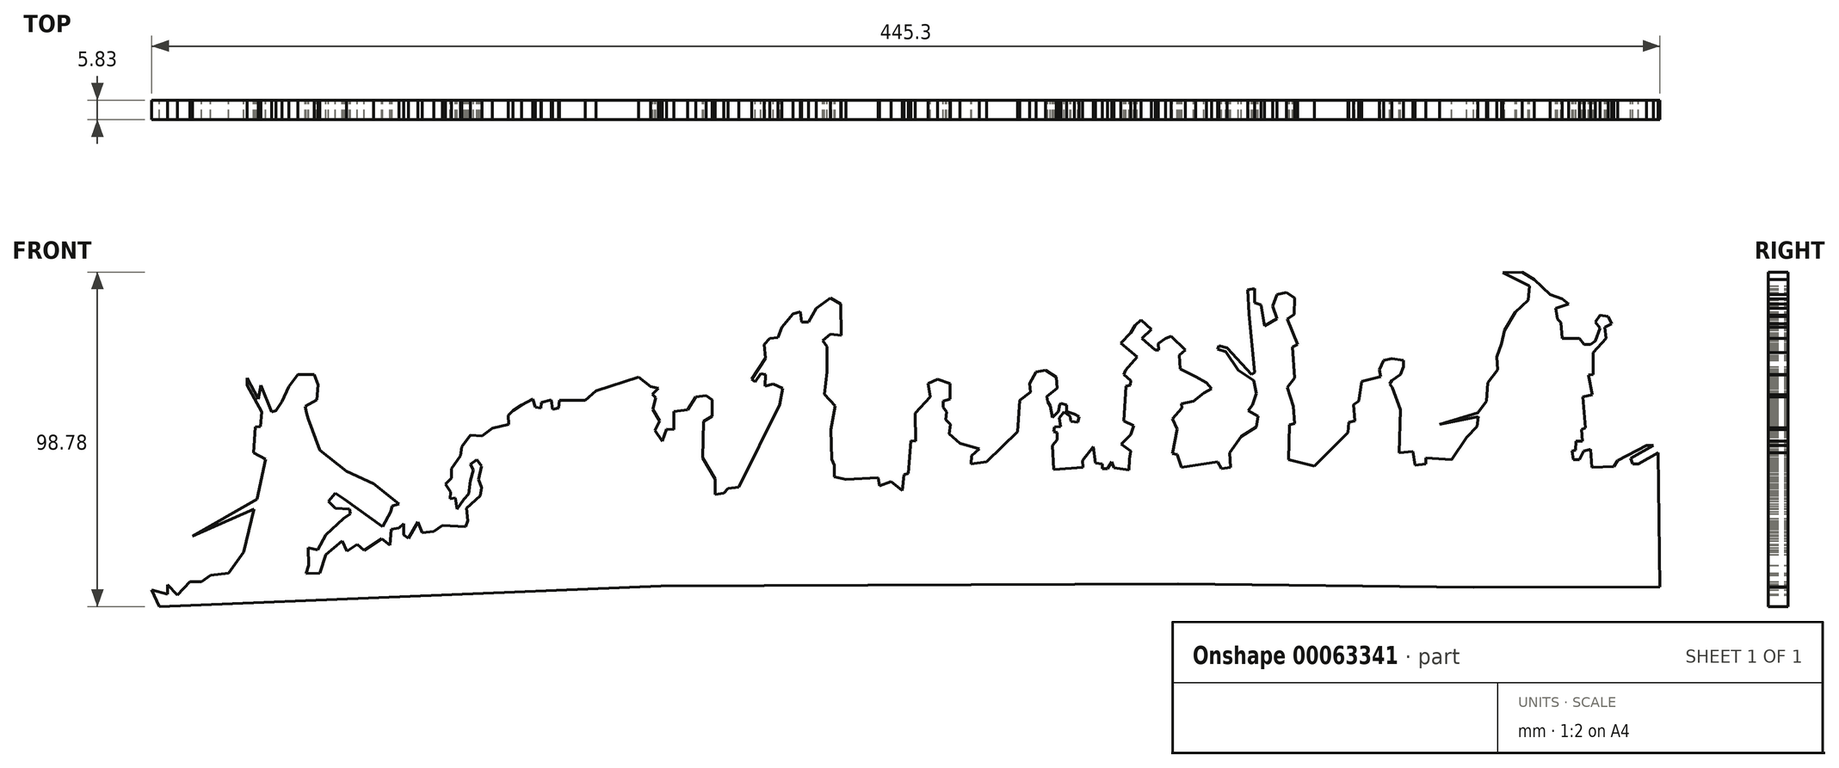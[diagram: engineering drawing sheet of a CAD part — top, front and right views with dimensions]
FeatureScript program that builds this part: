
annotation { "Feature Type Name" : "Feature", "Feature Type Description" : "" }
export const myFeature = defineFeature(function(context is Context, id is Id, definition is map)
    precondition{}
    {
        {
            var Q0;
            Q0=qCreatedBy(makeId("Front.planeOp"),FACE);
            var sketch = newSketch(context, id + "F0", { "sketchPlane" : qUnion([Q0])});
            skLineSegment(sketch, "E0", {"start": v(167.62, -43.74) * mm, "end": v(222.65, -43.54) * mm});
            skLineSegment(sketch, "E1", {"start": v(222.65, -43.54) * mm, "end": v(222.05, -4.03) * mm});
            skLineSegment(sketch, "E2", {"start": v(222.05, -4.03) * mm, "end": v(216.2, -7.26) * mm});
            skLineSegment(sketch, "E3", {"start": v(216.2, -7.26) * mm, "end": v(214.59, -7.26) * mm});
            skLineSegment(sketch, "E4", {"start": v(214.59, -7.26) * mm, "end": v(213.98, -5.64) * mm});
            skLineSegment(sketch, "E5", {"start": v(213.98, -5.64) * mm, "end": v(220.64, -1.81) * mm});
            skLineSegment(sketch, "E6", {"start": v(220.64, -1.81) * mm, "end": v(218.62, -1.81) * mm});
            skLineSegment(sketch, "E7", {"start": v(218.62, -1.81) * mm, "end": v(210.15, -6.25) * mm});
            skLineSegment(sketch, "E8", {"start": v(210.15, -6.25) * mm, "end": v(208.95, -8.06) * mm});
            skLineSegment(sketch, "E9", {"start": v(208.95, -8.06) * mm, "end": v(202.5, -8.27) * mm});
            skLineSegment(sketch, "E10", {"start": v(202.5, -8.27) * mm, "end": v(202.1, -3.02) * mm});
            skLineSegment(sketch, "E11", {"start": v(202.1, -3.02) * mm, "end": v(200.08, -3.43) * mm});
            skLineSegment(sketch, "E12", {"start": v(200.08, -3.43) * mm, "end": v(198.87, -6.05) * mm});
            skLineSegment(sketch, "E13", {"start": v(198.87, -6.05) * mm, "end": v(197.05, -6.05) * mm});
            skLineSegment(sketch, "E14", {"start": v(197.05, -6.05) * mm, "end": v(196.65, -3.43) * mm});
            skLineSegment(sketch, "E15", {"start": v(196.65, -3.43) * mm, "end": v(197.66, -3.23) * mm});
            skLineSegment(sketch, "E16", {"start": v(197.66, -3.23) * mm, "end": v(197.86, -0.6) * mm});
            skLineSegment(sketch, "E17", {"start": v(197.86, -0.6) * mm, "end": v(199.67, -0.6) * mm});
            skLineSegment(sketch, "E18", {"start": v(199.67, -0.6) * mm, "end": v(199.47, 2.82) * mm});
            skLineSegment(sketch, "E19", {"start": v(199.47, 2.82) * mm, "end": v(200.68, 3.43) * mm});
            skLineSegment(sketch, "E20", {"start": v(200.68, 3.43) * mm, "end": v(199.87, 12.5) * mm});
            skLineSegment(sketch, "E21", {"start": v(199.87, 12.5) * mm, "end": v(202.7, 13.1) * mm});
            skLineSegment(sketch, "E22", {"start": v(202.7, 13.1) * mm, "end": v(201.49, 18.95) * mm});
            skLineSegment(sketch, "E23", {"start": v(201.49, 18.95) * mm, "end": v(202.9, 19.15) * mm});
            skLineSegment(sketch, "E24", {"start": v(202.9, 19.15) * mm, "end": v(202.9, 25.6) * mm});
            skLineSegment(sketch, "E25", {"start": v(202.9, 25.6) * mm, "end": v(206.73, 29.83) * mm});
            skLineSegment(sketch, "E26", {"start": v(206.73, 29.83) * mm, "end": v(206.32, 33.06) * mm});
            skLineSegment(sketch, "E27", {"start": v(206.32, 33.06) * mm, "end": v(208.34, 34.07) * mm});
            skLineSegment(sketch, "E28", {"start": v(208.34, 34.07) * mm, "end": v(207.33, 36.29) * mm});
            skLineSegment(sketch, "E29", {"start": v(207.33, 36.29) * mm, "end": v(204.91, 36.69) * mm});
            skLineSegment(sketch, "E30", {"start": v(204.91, 36.69) * mm, "end": v(203.5, 34.67) * mm});
            skLineSegment(sketch, "E31", {"start": v(203.5, 34.67) * mm, "end": v(204.91, 32.86) * mm});
            skLineSegment(sketch, "E32", {"start": v(204.91, 32.86) * mm, "end": v(203.5, 29.03) * mm});
            skLineSegment(sketch, "E33", {"start": v(203.5, 29.03) * mm, "end": v(202.1, 28.02) * mm});
            skLineSegment(sketch, "E34", {"start": v(202.1, 28.02) * mm, "end": v(200.28, 28.02) * mm});
            skLineSegment(sketch, "E35", {"start": v(200.28, 28.02) * mm, "end": v(198.87, 29.83) * mm});
            skLineSegment(sketch, "E36", {"start": v(198.87, 29.83) * mm, "end": v(193.83, 29.83) * mm});
            skLineSegment(sketch, "E37", {"start": v(193.83, 29.83) * mm, "end": v(193.42, 34.47) * mm});
            skLineSegment(sketch, "E38", {"start": v(193.42, 34.47) * mm, "end": v(192.42, 35.48) * mm});
            skLineSegment(sketch, "E39", {"start": v(192.42, 35.48) * mm, "end": v(191.81, 38.7) * mm});
            skLineSegment(sketch, "E40", {"start": v(191.81, 38.7) * mm, "end": v(195.64, 39.91) * mm});
            skLineSegment(sketch, "E41", {"start": v(195.64, 39.91) * mm, "end": v(193.83, 41.53) * mm});
            skLineSegment(sketch, "E42", {"start": v(193.83, 41.53) * mm, "end": v(190.2, 42.74) * mm});
            skLineSegment(sketch, "E43", {"start": v(190.2, 42.74) * mm, "end": v(185.56, 47.17) * mm});
            skLineSegment(sketch, "E44", {"start": v(185.56, 47.17) * mm, "end": v(181.93, 49.39) * mm});
            skLineSegment(sketch, "E45", {"start": v(181.93, 49.39) * mm, "end": v(176.29, 49.19) * mm});
            skLineSegment(sketch, "E46", {"start": v(176.29, 49.19) * mm, "end": v(180.32, 47.17) * mm});
            skLineSegment(sketch, "E47", {"start": v(180.32, 47.17) * mm, "end": v(184.15, 45.36) * mm});
            skLineSegment(sketch, "E48", {"start": v(184.15, 45.36) * mm, "end": v(183.75, 41.12) * mm});
            skLineSegment(sketch, "E49", {"start": v(183.75, 41.12) * mm, "end": v(179.92, 37.5) * mm});
            skLineSegment(sketch, "E50", {"start": v(179.92, 37.5) * mm, "end": v(176.7, 32.25) * mm});
            skLineSegment(sketch, "E51", {"start": v(176.7, 32.25) * mm, "end": v(175.88, 28.22) * mm});
            skLineSegment(sketch, "E52", {"start": v(175.88, 28.22) * mm, "end": v(174.47, 24.4) * mm});
            skLineSegment(sketch, "E53", {"start": v(174.47, 24.4) * mm, "end": v(174.68, 20.56) * mm});
            skLineSegment(sketch, "E54", {"start": v(174.68, 20.56) * mm, "end": v(171.85, 16.73) * mm});
            skLineSegment(sketch, "E55", {"start": v(171.85, 16.73) * mm, "end": v(171.45, 11.29) * mm});
            skLineSegment(sketch, "E56", {"start": v(171.45, 11.29) * mm, "end": v(168.83, 7.86) * mm});
            skLineSegment(sketch, "E57", {"start": v(168.83, 7.86) * mm, "end": v(157.54, 4.43) * mm});
            skLineSegment(sketch, "E58", {"start": v(157.54, 4.43) * mm, "end": v(169.03, 6.65) * mm});
            skLineSegment(sketch, "E59", {"start": v(169.03, 6.65) * mm, "end": v(168.63, 3.83) * mm});
            skLineSegment(sketch, "E60", {"start": v(168.63, 3.83) * mm, "end": v(165.6, 0.6) * mm});
            skLineSegment(sketch, "E61", {"start": v(165.6, 0.6) * mm, "end": v(161.17, -6.05) * mm});
            skLineSegment(sketch, "E62", {"start": v(161.17, -6.05) * mm, "end": v(153.5, -5.44) * mm});
            skLineSegment(sketch, "E63", {"start": v(153.5, -5.44) * mm, "end": v(153.5, -7.26) * mm});
            skLineSegment(sketch, "E64", {"start": v(153.5, -7.26) * mm, "end": v(150.28, -7.66) * mm});
            skLineSegment(sketch, "E65", {"start": v(150.28, -7.66) * mm, "end": v(149.68, -3.63) * mm});
            skLineSegment(sketch, "E66", {"start": v(149.68, -3.63) * mm, "end": v(145.65, -4.03) * mm});
            skLineSegment(sketch, "E67", {"start": v(145.65, -4.03) * mm, "end": v(146.05, 8.67) * mm});
            skLineSegment(sketch, "E68", {"start": v(146.05, 8.67) * mm, "end": v(143.63, 15.32) * mm});
            skLineSegment(sketch, "E69", {"start": v(143.63, 15.32) * mm, "end": v(142.82, 16.33) * mm});
            skLineSegment(sketch, "E70", {"start": v(142.82, 16.33) * mm, "end": v(143.43, 17.34) * mm});
            skLineSegment(sketch, "E71", {"start": v(143.43, 17.34) * mm, "end": v(146.05, 19.15) * mm});
            skLineSegment(sketch, "E72", {"start": v(146.05, 19.15) * mm, "end": v(146.86, 21.37) * mm});
            skLineSegment(sketch, "E73", {"start": v(146.86, 21.37) * mm, "end": v(146.86, 23.38) * mm});
            skLineSegment(sketch, "E74", {"start": v(146.86, 23.38) * mm, "end": v(143.43, 23.79) * mm});
            skLineSegment(sketch, "E75", {"start": v(143.43, 23.79) * mm, "end": v(141.01, 23.38) * mm});
            skLineSegment(sketch, "E76", {"start": v(141.01, 23.38) * mm, "end": v(139.8, 20.56) * mm});
            skLineSegment(sketch, "E77", {"start": v(139.8, 20.56) * mm, "end": v(140.2, 18.55) * mm});
            skLineSegment(sketch, "E78", {"start": v(140.2, 18.55) * mm, "end": v(134.56, 17.13) * mm});
            skLineSegment(sketch, "E79", {"start": v(134.56, 17.13) * mm, "end": v(133.75, 11.29) * mm});
            skLineSegment(sketch, "E80", {"start": v(133.75, 11.29) * mm, "end": v(132.14, 10.28) * mm});
            skLineSegment(sketch, "E81", {"start": v(132.14, 10.28) * mm, "end": v(132.54, 5.44) * mm});
            skLineSegment(sketch, "E82", {"start": v(132.54, 5.44) * mm, "end": v(130.73, 5.04) * mm});
            skLineSegment(sketch, "E83", {"start": v(130.73, 5.04) * mm, "end": v(130.53, 2.02) * mm});
            skLineSegment(sketch, "E84", {"start": v(130.53, 2.02) * mm, "end": v(120.65, -7.86) * mm});
            skLineSegment(sketch, "E85", {"start": v(120.65, -7.86) * mm, "end": v(112.99, -6.05) * mm});
            skLineSegment(sketch, "E86", {"start": v(112.99, -6.05) * mm, "end": v(113.2, 4.23) * mm});
            skLineSegment(sketch, "E87", {"start": v(113.2, 4.23) * mm, "end": v(114.8, 4.64) * mm});
            skLineSegment(sketch, "E88", {"start": v(114.8, 4.64) * mm, "end": v(114.4, 9.68) * mm});
            skLineSegment(sketch, "E89", {"start": v(114.4, 9.68) * mm, "end": v(112.59, 15.32) * mm});
            skLineSegment(sketch, "E90", {"start": v(112.59, 15.32) * mm, "end": v(114.8, 18.14) * mm});
            skLineSegment(sketch, "E91", {"start": v(114.8, 18.14) * mm, "end": v(114.2, 27.21) * mm});
            skLineSegment(sketch, "E92", {"start": v(114.2, 27.21) * mm, "end": v(115.61, 28.02) * mm});
            skLineSegment(sketch, "E93", {"start": v(115.61, 28.02) * mm, "end": v(112.59, 35.48) * mm});
            skLineSegment(sketch, "E94", {"start": v(112.59, 35.48) * mm, "end": v(114.6, 36.9) * mm});
            skLineSegment(sketch, "E95", {"start": v(114.6, 36.9) * mm, "end": v(114.8, 41.73) * mm});
            skLineSegment(sketch, "E96", {"start": v(114.8, 41.73) * mm, "end": v(112.38, 43.34) * mm});
            skLineSegment(sketch, "E97", {"start": v(112.38, 43.34) * mm, "end": v(109.56, 42.74) * mm});
            skLineSegment(sketch, "E98", {"start": v(109.56, 42.74) * mm, "end": v(108.35, 39.3) * mm});
            skLineSegment(sketch, "E99", {"start": v(108.35, 39.3) * mm, "end": v(109.56, 35.68) * mm});
            skLineSegment(sketch, "E100", {"start": v(109.56, 35.68) * mm, "end": v(105.93, 33.46) * mm});
            skLineSegment(sketch, "E101", {"start": v(105.93, 33.46) * mm, "end": v(104.93, 39.71) * mm});
            skLineSegment(sketch, "E102", {"start": v(104.93, 39.71) * mm, "end": v(102.91, 40.32) * mm});
            skLineSegment(sketch, "E103", {"start": v(102.91, 40.32) * mm, "end": v(102.91, 44.55) * mm});
            skLineSegment(sketch, "E104", {"start": v(102.91, 44.55) * mm, "end": v(100.9, 44.15) * mm});
            skLineSegment(sketch, "E105", {"start": v(100.9, 44.15) * mm, "end": v(101.3, 37.1) * mm});
            skLineSegment(sketch, "E106", {"start": v(101.3, 37.1) * mm, "end": v(102.91, 19.76) * mm});
            skLineSegment(sketch, "E107", {"start": v(102.91, 19.76) * mm, "end": v(102.1, 19.15) * mm});
            skLineSegment(sketch, "E108", {"start": v(102.1, 19.15) * mm, "end": v(94.85, 27.01) * mm});
            skLineSegment(sketch, "E109", {"start": v(94.85, 27.01) * mm, "end": v(92.43, 27.62) * mm});
            skLineSegment(sketch, "E110", {"start": v(92.43, 27.62) * mm, "end": v(92.02, 26.6) * mm});
            skLineSegment(sketch, "E111", {"start": v(92.02, 26.6) * mm, "end": v(94.44, 25.8) * mm});
            skLineSegment(sketch, "E112", {"start": v(94.44, 25.8) * mm, "end": v(98.07, 20.36) * mm});
            skLineSegment(sketch, "E113", {"start": v(98.07, 20.36) * mm, "end": v(102.7, 17.34) * mm});
            skLineSegment(sketch, "E114", {"start": v(102.7, 17.34) * mm, "end": v(103.52, 13.5) * mm});
            skLineSegment(sketch, "E115", {"start": v(103.52, 13.5) * mm, "end": v(102.3, 10.08) * mm});
            skLineSegment(sketch, "E116", {"start": v(102.3, 10.08) * mm, "end": v(101.1, 8.47) * mm});
            skLineSegment(sketch, "E117", {"start": v(101.1, 8.47) * mm, "end": v(103.92, 6.85) * mm});
            skLineSegment(sketch, "E118", {"start": v(103.92, 6.85) * mm, "end": v(103.52, 3.63) * mm});
            skLineSegment(sketch, "E119", {"start": v(103.52, 3.63) * mm, "end": v(99.08, 0.8) * mm});
            skLineSegment(sketch, "E120", {"start": v(99.08, 0.8) * mm, "end": v(95.65, -4.03) * mm});
            skLineSegment(sketch, "E121", {"start": v(95.65, -4.03) * mm, "end": v(95.85, -8.27) * mm});
            skLineSegment(sketch, "E122", {"start": v(95.85, -8.27) * mm, "end": v(93.23, -8.67) * mm});
            skLineSegment(sketch, "E123", {"start": v(93.23, -8.67) * mm, "end": v(92.02, -6.65) * mm});
            skLineSegment(sketch, "E124", {"start": v(92.02, -6.65) * mm, "end": v(81.34, -8.27) * mm});
            skLineSegment(sketch, "E125", {"start": v(81.34, -8.27) * mm, "end": v(80.13, -4.43) * mm});
            skLineSegment(sketch, "E126", {"start": v(80.13, -4.43) * mm, "end": v(78.72, -4.23) * mm});
            skLineSegment(sketch, "E127", {"start": v(78.72, -4.23) * mm, "end": v(80.13, 3.02) * mm});
            skLineSegment(sketch, "E128", {"start": v(80.13, 3.02) * mm, "end": v(78.72, 6.05) * mm});
            skLineSegment(sketch, "E129", {"start": v(78.72, 6.05) * mm, "end": v(81.54, 9.27) * mm});
            skLineSegment(sketch, "E130", {"start": v(81.54, 9.27) * mm, "end": v(81.34, 10.48) * mm});
            skLineSegment(sketch, "E131", {"start": v(81.34, 10.48) * mm, "end": v(84.97, 11.29) * mm});
            skLineSegment(sketch, "E132", {"start": v(84.97, 11.29) * mm, "end": v(88, 13.7) * mm});
            skLineSegment(sketch, "E133", {"start": v(88, 13.7) * mm, "end": v(90.21, 14.92) * mm});
            skLineSegment(sketch, "E134", {"start": v(90.21, 14.92) * mm, "end": v(88.8, 16.73) * mm});
            skLineSegment(sketch, "E135", {"start": v(88.8, 16.73) * mm, "end": v(85.57, 18.55) * mm});
            skLineSegment(sketch, "E136", {"start": v(85.57, 18.55) * mm, "end": v(80.94, 20.76) * mm});
            skLineSegment(sketch, "E137", {"start": v(80.94, 20.76) * mm, "end": v(80.74, 24.8) * mm});
            skLineSegment(sketch, "E138", {"start": v(80.74, 24.8) * mm, "end": v(82.55, 26.4) * mm});
            skLineSegment(sketch, "E139", {"start": v(82.55, 26.4) * mm, "end": v(78.32, 30.44) * mm});
            skLineSegment(sketch, "E140", {"start": v(78.32, 30.44) * mm, "end": v(76.7, 29.83) * mm});
            skLineSegment(sketch, "E141", {"start": v(76.7, 29.83) * mm, "end": v(74.49, 28.22) * mm});
            skLineSegment(sketch, "E142", {"start": v(74.49, 28.22) * mm, "end": v(74.69, 26.4) * mm});
            skLineSegment(sketch, "E143", {"start": v(74.69, 26.4) * mm, "end": v(73.68, 26.4) * mm});
            skLineSegment(sketch, "E144", {"start": v(73.68, 26.4) * mm, "end": v(69.65, 29.83) * mm});
            skLineSegment(sketch, "E145", {"start": v(69.65, 29.83) * mm, "end": v(72.47, 32.46) * mm});
            skLineSegment(sketch, "E146", {"start": v(72.47, 32.46) * mm, "end": v(69.45, 35.28) * mm});
            skLineSegment(sketch, "E147", {"start": v(69.45, 35.28) * mm, "end": v(67.63, 33.67) * mm});
            skLineSegment(sketch, "E148", {"start": v(67.63, 33.67) * mm, "end": v(66.42, 31.45) * mm});
            skLineSegment(sketch, "E149", {"start": v(66.42, 31.45) * mm, "end": v(63.4, 28.42) * mm});
            skLineSegment(sketch, "E150", {"start": v(63.4, 28.42) * mm, "end": v(68.24, 24.4) * mm});
            skLineSegment(sketch, "E151", {"start": v(68.24, 24.4) * mm, "end": v(64.81, 20.36) * mm});
            skLineSegment(sketch, "E152", {"start": v(64.81, 20.36) * mm, "end": v(64.4, 19.15) * mm});
            skLineSegment(sketch, "E153", {"start": v(64.4, 19.15) * mm, "end": v(66.42, 17.34) * mm});
            skLineSegment(sketch, "E154", {"start": v(66.42, 17.34) * mm, "end": v(66.22, 15.93) * mm});
            skLineSegment(sketch, "E155", {"start": v(66.22, 15.93) * mm, "end": v(65.01, 15.72) * mm});
            skLineSegment(sketch, "E156", {"start": v(65.01, 15.72) * mm, "end": v(64.4, 5.44) * mm});
            skLineSegment(sketch, "E157", {"start": v(64.4, 5.44) * mm, "end": v(67.23, 4.03) * mm});
            skLineSegment(sketch, "E158", {"start": v(67.23, 4.03) * mm, "end": v(66.42, 1.41) * mm});
            skLineSegment(sketch, "E159", {"start": v(66.42, 1.41) * mm, "end": v(63.6, -1.41) * mm});
            skLineSegment(sketch, "E160", {"start": v(63.6, -1.41) * mm, "end": v(66.42, -3.43) * mm});
            skLineSegment(sketch, "E161", {"start": v(66.42, -3.43) * mm, "end": v(66.02, -5.85) * mm});
            skLineSegment(sketch, "E162", {"start": v(66.02, -5.85) * mm, "end": v(65.82, -9.07) * mm});
            skLineSegment(sketch, "E163", {"start": v(65.82, -9.07) * mm, "end": v(61.38, -8.47) * mm});
            skLineSegment(sketch, "E164", {"start": v(61.38, -8.47) * mm, "end": v(60.78, -6.65) * mm});
            skLineSegment(sketch, "E165", {"start": v(60.78, -6.65) * mm, "end": v(59.57, -8.67) * mm});
            skLineSegment(sketch, "E166", {"start": v(59.57, -8.67) * mm, "end": v(57.96, -8.67) * mm});
            skLineSegment(sketch, "E167", {"start": v(57.96, -8.67) * mm, "end": v(57.96, -7.26) * mm});
            skLineSegment(sketch, "E168", {"start": v(57.96, -7.26) * mm, "end": v(55.94, -7.06) * mm});
            skLineSegment(sketch, "E169", {"start": v(55.94, -7.06) * mm, "end": v(55.34, -2.22) * mm});
            skLineSegment(sketch, "E170", {"start": v(55.34, -2.22) * mm, "end": v(52.11, -6.25) * mm});
            skLineSegment(sketch, "E171", {"start": v(52.11, -6.25) * mm, "end": v(52.31, -8.27) * mm});
            skLineSegment(sketch, "E172", {"start": v(52.31, -8.27) * mm, "end": v(43.64, -8.87) * mm});
            skLineSegment(sketch, "E173", {"start": v(43.64, -8.87) * mm, "end": v(43.24, -1.81) * mm});
            skLineSegment(sketch, "E174", {"start": v(43.24, -1.81) * mm, "end": v(44.65, -0.2) * mm});
            skLineSegment(sketch, "E175", {"start": v(44.65, -0.2) * mm, "end": v(44.65, 2.02) * mm});
            skLineSegment(sketch, "E176", {"start": v(44.65, 2.02) * mm, "end": v(43.64, 2.22) * mm});
            skLineSegment(sketch, "E177", {"start": v(43.64, 2.22) * mm, "end": v(43.85, 3.63) * mm});
            skLineSegment(sketch, "E178", {"start": v(43.85, 3.63) * mm, "end": v(45.66, 3.83) * mm});
            skLineSegment(sketch, "E179", {"start": v(45.66, 3.83) * mm, "end": v(45.26, 6.25) * mm});
            skLineSegment(sketch, "E180", {"start": v(45.26, 6.25) * mm, "end": v(46.67, 8.06) * mm});
            skLineSegment(sketch, "E181", {"start": v(46.67, 8.06) * mm, "end": v(48.48, 6.85) * mm});
            skLineSegment(sketch, "E182", {"start": v(48.48, 6.85) * mm, "end": v(48.68, 5.24) * mm});
            skLineSegment(sketch, "E183", {"start": v(48.68, 5.24) * mm, "end": v(50.7, 5.04) * mm});
            skLineSegment(sketch, "E184", {"start": v(50.7, 5.04) * mm, "end": v(51.1, 6.65) * mm});
            skLineSegment(sketch, "E185", {"start": v(51.1, 6.65) * mm, "end": v(49.7, 7.46) * mm});
            skLineSegment(sketch, "E186", {"start": v(49.7, 7.46) * mm, "end": v(47.47, 8.27) * mm});
            skLineSegment(sketch, "E187", {"start": v(47.47, 8.27) * mm, "end": v(47.47, 10.08) * mm});
            skLineSegment(sketch, "E188", {"start": v(47.47, 10.08) * mm, "end": v(45.86, 10.68) * mm});
            skLineSegment(sketch, "E189", {"start": v(45.86, 10.68) * mm, "end": v(45.46, 10.28) * mm});
            skLineSegment(sketch, "E190", {"start": v(45.46, 10.28) * mm, "end": v(45.05, 8.27) * mm});
            skLineSegment(sketch, "E191", {"start": v(45.05, 8.27) * mm, "end": v(43.24, 6.45) * mm});
            skLineSegment(sketch, "E192", {"start": v(43.24, 6.45) * mm, "end": v(42.64, 9.88) * mm});
            skLineSegment(sketch, "E193", {"start": v(42.64, 9.88) * mm, "end": v(41.83, 11.09) * mm});
            skLineSegment(sketch, "E194", {"start": v(41.83, 11.09) * mm, "end": v(41.63, 12.7) * mm});
            skLineSegment(sketch, "E195", {"start": v(41.63, 12.7) * mm, "end": v(44.65, 15.12) * mm});
            skLineSegment(sketch, "E196", {"start": v(44.65, 15.12) * mm, "end": v(44.45, 18.34) * mm});
            skLineSegment(sketch, "E197", {"start": v(44.45, 18.34) * mm, "end": v(41.22, 20.36) * mm});
            skLineSegment(sketch, "E198", {"start": v(41.22, 20.36) * mm, "end": v(38.4, 19.96) * mm});
            skLineSegment(sketch, "E199", {"start": v(38.4, 19.96) * mm, "end": v(36.59, 16.53) * mm});
            skLineSegment(sketch, "E200", {"start": v(36.59, 16.53) * mm, "end": v(36.79, 13.9) * mm});
            skLineSegment(sketch, "E201", {"start": v(36.79, 13.9) * mm, "end": v(33.56, 11.5) * mm});
            skLineSegment(sketch, "E202", {"start": v(33.56, 11.5) * mm, "end": v(32.96, 2.22) * mm});
            skLineSegment(sketch, "E203", {"start": v(32.96, 2.22) * mm, "end": v(23.89, -6.65) * mm});
            skLineSegment(sketch, "E204", {"start": v(23.89, -6.65) * mm, "end": v(19.25, -7.26) * mm});
            skLineSegment(sketch, "E205", {"start": v(19.25, -7.26) * mm, "end": v(19.45, -4.84) * mm});
            skLineSegment(sketch, "E206", {"start": v(19.45, -4.84) * mm, "end": v(21.67, -2.82) * mm});
            skLineSegment(sketch, "E207", {"start": v(21.67, -2.82) * mm, "end": v(16.03, -1.2) * mm});
            skLineSegment(sketch, "E208", {"start": v(16.03, -1.2) * mm, "end": v(12.8, 1.61) * mm});
            skLineSegment(sketch, "E209", {"start": v(12.8, 1.61) * mm, "end": v(13.2, 4.43) * mm});
            skLineSegment(sketch, "E210", {"start": v(13.2, 4.43) * mm, "end": v(11.8, 5.85) * mm});
            skLineSegment(sketch, "E211", {"start": v(11.8, 5.85) * mm, "end": v(12, 8.06) * mm});
            skLineSegment(sketch, "E212", {"start": v(12, 8.06) * mm, "end": v(10.99, 9.47) * mm});
            skLineSegment(sketch, "E213", {"start": v(10.99, 9.47) * mm, "end": v(10.99, 11.29) * mm});
            skLineSegment(sketch, "E214", {"start": v(10.99, 11.29) * mm, "end": v(13, 11.9) * mm});
            skLineSegment(sketch, "E215", {"start": v(13, 11.9) * mm, "end": v(13, 16.53) * mm});
            skLineSegment(sketch, "E216", {"start": v(13, 16.53) * mm, "end": v(9.37, 17.74) * mm});
            skLineSegment(sketch, "E217", {"start": v(9.37, 17.74) * mm, "end": v(6.55, 16.53) * mm});
            skLineSegment(sketch, "E218", {"start": v(6.55, 16.53) * mm, "end": v(7.16, 12.5) * mm});
            skLineSegment(sketch, "E219", {"start": v(7.16, 12.5) * mm, "end": v(2.72, 7.66) * mm});
            skLineSegment(sketch, "E220", {"start": v(2.72, 7.66) * mm, "end": v(2.92, -0.6) * mm});
            skLineSegment(sketch, "E221", {"start": v(2.92, -0.6) * mm, "end": v(1.51, -0.4) * mm});
            skLineSegment(sketch, "E222", {"start": v(1.51, -0.4) * mm, "end": v(0.7, -10.08) * mm});
            skLineSegment(sketch, "E223", {"start": v(0.7, -10.08) * mm, "end": v(-0.5, -10.48) * mm});
            skLineSegment(sketch, "E224", {"start": v(-0.5, -10.48) * mm, "end": v(-1.1, -15.12) * mm});
            skLineSegment(sketch, "E225", {"start": v(-1.1, -15.12) * mm, "end": v(-4.33, -12.5) * mm});
            skLineSegment(sketch, "E226", {"start": v(-4.33, -12.5) * mm, "end": v(-7.76, -13.7) * mm});
            skLineSegment(sketch, "E227", {"start": v(-7.76, -13.7) * mm, "end": v(-8.16, -11.29) * mm});
            skLineSegment(sketch, "E228", {"start": v(-8.16, -11.29) * mm, "end": v(-17.64, -11.9) * mm});
            skLineSegment(sketch, "E229", {"start": v(-17.64, -11.9) * mm, "end": v(-21.07, -11.09) * mm});
            skLineSegment(sketch, "E230", {"start": v(-21.07, -11.09) * mm, "end": v(-21.07, -7.66) * mm});
            skLineSegment(sketch, "E231", {"start": v(-21.07, -7.66) * mm, "end": v(-21.87, -5.85) * mm});
            skLineSegment(sketch, "E232", {"start": v(-21.87, -5.85) * mm, "end": v(-22.07, 2.82) * mm});
            skLineSegment(sketch, "E233", {"start": v(-22.07, 2.82) * mm, "end": v(-20.86, 9.88) * mm});
            skLineSegment(sketch, "E234", {"start": v(-20.86, 9.88) * mm, "end": v(-24.09, 13.3) * mm});
            skLineSegment(sketch, "E235", {"start": v(-24.09, 13.3) * mm, "end": v(-23.28, 19.96) * mm});
            skLineSegment(sketch, "E236", {"start": v(-23.28, 19.96) * mm, "end": v(-23.28, 27.42) * mm});
            skLineSegment(sketch, "E237", {"start": v(-23.28, 27.42) * mm, "end": v(-24.5, 29.23) * mm});
            skLineSegment(sketch, "E238", {"start": v(-24.5, 29.23) * mm, "end": v(-22.28, 31.04) * mm});
            skLineSegment(sketch, "E239", {"start": v(-22.28, 31.04) * mm, "end": v(-19.05, 30.64) * mm});
            skLineSegment(sketch, "E240", {"start": v(-19.05, 30.64) * mm, "end": v(-19.25, 39.91) * mm});
            skLineSegment(sketch, "E241", {"start": v(-19.25, 39.91) * mm, "end": v(-22.28, 41.73) * mm});
            skLineSegment(sketch, "E242", {"start": v(-22.28, 41.73) * mm, "end": v(-26.5, 38.7) * mm});
            skLineSegment(sketch, "E243", {"start": v(-26.5, 38.7) * mm, "end": v(-28.73, 34.67) * mm});
            skLineSegment(sketch, "E244", {"start": v(-28.73, 34.67) * mm, "end": v(-30.74, 34.67) * mm});
            skLineSegment(sketch, "E245", {"start": v(-30.74, 34.67) * mm, "end": v(-31.15, 37.7) * mm});
            skLineSegment(sketch, "E246", {"start": v(-31.15, 37.7) * mm, "end": v(-33.36, 37.1) * mm});
            skLineSegment(sketch, "E247", {"start": v(-33.36, 37.1) * mm, "end": v(-36.59, 33.06) * mm});
            skLineSegment(sketch, "E248", {"start": v(-36.59, 33.06) * mm, "end": v(-37.8, 30.04) * mm});
            skLineSegment(sketch, "E249", {"start": v(-37.8, 30.04) * mm, "end": v(-40.22, 29.83) * mm});
            skLineSegment(sketch, "E250", {"start": v(-40.22, 29.83) * mm, "end": v(-41.83, 28.02) * mm});
            skLineSegment(sketch, "E251", {"start": v(-41.83, 28.02) * mm, "end": v(-41.43, 23.99) * mm});
            skLineSegment(sketch, "E252", {"start": v(-41.43, 23.99) * mm, "end": v(-45.46, 17.74) * mm});
            skLineSegment(sketch, "E253", {"start": v(-45.46, 17.74) * mm, "end": v(-44.45, 16.93) * mm});
            skLineSegment(sketch, "E254", {"start": v(-44.45, 16.93) * mm, "end": v(-42.84, 19.35) * mm});
            skLineSegment(sketch, "E255", {"start": v(-42.84, 19.35) * mm, "end": v(-41.43, 19.15) * mm});
            skLineSegment(sketch, "E256", {"start": v(-41.43, 19.15) * mm, "end": v(-41.63, 15.72) * mm});
            skLineSegment(sketch, "E257", {"start": v(-41.63, 15.72) * mm, "end": v(-39.2, 16.33) * mm});
            skLineSegment(sketch, "E258", {"start": v(-39.2, 16.33) * mm, "end": v(-36.39, 15.12) * mm});
            skLineSegment(sketch, "E259", {"start": v(-36.39, 15.12) * mm, "end": v(-37.2, 10.28) * mm});
            skLineSegment(sketch, "E260", {"start": v(-37.2, 10.28) * mm, "end": v(-49.29, -14.11) * mm});
            skLineSegment(sketch, "E261", {"start": v(-49.29, -14.11) * mm, "end": v(-52.51, -14.51) * mm});
            skLineSegment(sketch, "E262", {"start": v(-52.51, -14.51) * mm, "end": v(-53.72, -15.93) * mm});
            skLineSegment(sketch, "E263", {"start": v(-53.72, -15.93) * mm, "end": v(-56.34, -16.33) * mm});
            skLineSegment(sketch, "E264", {"start": v(-56.34, -16.33) * mm, "end": v(-56.34, -11.7) * mm});
            skLineSegment(sketch, "E265", {"start": v(-56.34, -11.7) * mm, "end": v(-59.97, -5.44) * mm});
            skLineSegment(sketch, "E266", {"start": v(-59.97, -5.44) * mm, "end": v(-59.77, 5.24) * mm});
            skLineSegment(sketch, "E267", {"start": v(-59.77, 5.24) * mm, "end": v(-57.15, 6.85) * mm});
            skLineSegment(sketch, "E268", {"start": v(-57.15, 6.85) * mm, "end": v(-57.15, 11.7) * mm});
            skLineSegment(sketch, "E269", {"start": v(-57.15, 11.7) * mm, "end": v(-58.96, 12.9) * mm});
            skLineSegment(sketch, "E270", {"start": v(-58.96, 12.9) * mm, "end": v(-61.99, 12.5) * mm});
            skLineSegment(sketch, "E271", {"start": v(-61.99, 12.5) * mm, "end": v(-64.4, 8.67) * mm});
            skLineSegment(sketch, "E272", {"start": v(-64.4, 8.67) * mm, "end": v(-68.44, 8.27) * mm});
            skLineSegment(sketch, "E273", {"start": v(-68.44, 8.27) * mm, "end": v(-68.44, 2.82) * mm});
            skLineSegment(sketch, "E274", {"start": v(-68.44, 2.82) * mm, "end": v(-70.66, 3.02) * mm});
            skLineSegment(sketch, "E275", {"start": v(-70.66, 3.02) * mm, "end": v(-71.87, -0.6) * mm});
            skLineSegment(sketch, "E276", {"start": v(-71.87, -0.6) * mm, "end": v(-74.08, 2.62) * mm});
            skLineSegment(sketch, "E277", {"start": v(-74.08, 2.62) * mm, "end": v(-72.67, 5.44) * mm});
            skLineSegment(sketch, "E278", {"start": v(-72.67, 5.44) * mm, "end": v(-74.69, 8.87) * mm});
            skLineSegment(sketch, "E279", {"start": v(-74.69, 8.87) * mm, "end": v(-73.88, 12.3) * mm});
            skLineSegment(sketch, "E280", {"start": v(-73.88, 12.3) * mm, "end": v(-74.89, 13.3) * mm});
            skLineSegment(sketch, "E281", {"start": v(-74.89, 13.3) * mm, "end": v(-73.08, 15.12) * mm});
            skLineSegment(sketch, "E282", {"start": v(-73.08, 15.12) * mm, "end": v(-75.3, 15.52) * mm});
            skLineSegment(sketch, "E283", {"start": v(-75.3, 15.52) * mm, "end": v(-78.92, 18.34) * mm});
            skLineSegment(sketch, "E284", {"start": v(-78.92, 18.34) * mm, "end": v(-91.42, 14.31) * mm});
            skLineSegment(sketch, "E285", {"start": v(-91.42, 14.31) * mm, "end": v(-94.65, 11.5) * mm});
            skLineSegment(sketch, "E286", {"start": v(-94.65, 11.5) * mm, "end": v(-102.3, 11.5) * mm});
            skLineSegment(sketch, "E287", {"start": v(-102.3, 11.5) * mm, "end": v(-102.5, 9.27) * mm});
            skLineSegment(sketch, "E288", {"start": v(-102.5, 9.27) * mm, "end": v(-104.32, 8.87) * mm});
            skLineSegment(sketch, "E289", {"start": v(-104.32, 8.87) * mm, "end": v(-104.72, 11.7) * mm});
            skLineSegment(sketch, "E290", {"start": v(-104.72, 11.7) * mm, "end": v(-107.55, 10.89) * mm});
            skLineSegment(sketch, "E291", {"start": v(-107.55, 10.89) * mm, "end": v(-107.75, 9.27) * mm});
            skLineSegment(sketch, "E292", {"start": v(-107.75, 9.27) * mm, "end": v(-109.36, 9.47) * mm});
            skLineSegment(sketch, "E293", {"start": v(-109.36, 9.47) * mm, "end": v(-110.17, 11.9) * mm});
            skLineSegment(sketch, "E294", {"start": v(-110.17, 11.9) * mm, "end": v(-113.4, 10.08) * mm});
            skLineSegment(sketch, "E295", {"start": v(-113.4, 10.08) * mm, "end": v(-116.01, 8.47) * mm});
            skLineSegment(sketch, "E296", {"start": v(-116.01, 8.47) * mm, "end": v(-117.42, 7.06) * mm});
            skLineSegment(sketch, "E297", {"start": v(-117.42, 7.06) * mm, "end": v(-117.22, 4.43) * mm});
            skLineSegment(sketch, "E298", {"start": v(-117.22, 4.43) * mm, "end": v(-122.06, 3.23) * mm});
            skLineSegment(sketch, "E299", {"start": v(-122.06, 3.23) * mm, "end": v(-125.08, 1) * mm});
            skLineSegment(sketch, "E300", {"start": v(-125.08, 1) * mm, "end": v(-128.51, 1.2) * mm});
            skLineSegment(sketch, "E301", {"start": v(-128.51, 1.2) * mm, "end": v(-131.13, -2.22) * mm});
            skLineSegment(sketch, "E302", {"start": v(-131.13, -2.22) * mm, "end": v(-131.54, -4.84) * mm});
            skLineSegment(sketch, "E303", {"start": v(-131.54, -4.84) * mm, "end": v(-134.16, -8.67) * mm});
            skLineSegment(sketch, "E304", {"start": v(-134.16, -8.67) * mm, "end": v(-134.16, -11.5) * mm});
            skLineSegment(sketch, "E305", {"start": v(-134.16, -11.5) * mm, "end": v(-135.97, -13.3) * mm});
            skLineSegment(sketch, "E306", {"start": v(-135.97, -13.3) * mm, "end": v(-134.36, -15.52) * mm});
            skLineSegment(sketch, "E307", {"start": v(-134.36, -15.52) * mm, "end": v(-134.56, -17.54) * mm});
            skLineSegment(sketch, "E308", {"start": v(-134.56, -17.54) * mm, "end": v(-132.95, -17.34) * mm});
            skLineSegment(sketch, "E309", {"start": v(-132.95, -17.34) * mm, "end": v(-132.54, -20.56) * mm});
            skLineSegment(sketch, "E310", {"start": v(-132.54, -20.56) * mm, "end": v(-130.53, -17.74) * mm});
            skLineSegment(sketch, "E311", {"start": v(-130.53, -17.74) * mm, "end": v(-129.12, -16.13) * mm});
            skLineSegment(sketch, "E312", {"start": v(-129.12, -16.13) * mm, "end": v(-128.51, -12.3) * mm});
            skLineSegment(sketch, "E313", {"start": v(-128.51, -12.3) * mm, "end": v(-127.7, -9.07) * mm});
            skLineSegment(sketch, "E314", {"start": v(-127.7, -9.07) * mm, "end": v(-128.51, -7.46) * mm});
            skLineSegment(sketch, "E315", {"start": v(-128.51, -7.46) * mm, "end": v(-126.7, -6.05) * mm});
            skLineSegment(sketch, "E316", {"start": v(-126.7, -6.05) * mm, "end": v(-125.29, -7.86) * mm});
            skLineSegment(sketch, "E317", {"start": v(-125.29, -7.86) * mm, "end": v(-126.1, -11.9) * mm});
            skLineSegment(sketch, "E318", {"start": v(-126.1, -11.9) * mm, "end": v(-125.29, -14.31) * mm});
            skLineSegment(sketch, "E319", {"start": v(-125.29, -14.31) * mm, "end": v(-125.69, -16.73) * mm});
            skLineSegment(sketch, "E320", {"start": v(-125.69, -16.73) * mm, "end": v(-129.72, -20.36) * mm});
            skLineSegment(sketch, "E321", {"start": v(-129.72, -20.36) * mm, "end": v(-129.32, -23.99) * mm});
            skLineSegment(sketch, "E322", {"start": v(-129.32, -23.99) * mm, "end": v(-129.92, -25.8) * mm});
            skLineSegment(sketch, "E323", {"start": v(-129.92, -25.8) * mm, "end": v(-136.78, -25.4) * mm});
            skLineSegment(sketch, "E324", {"start": v(-136.78, -25.4) * mm, "end": v(-139.4, -27.21) * mm});
            skLineSegment(sketch, "E325", {"start": v(-139.4, -27.21) * mm, "end": v(-142.82, -27.62) * mm});
            skLineSegment(sketch, "E326", {"start": v(-142.82, -27.62) * mm, "end": v(-144.03, -24.4) * mm});
            skLineSegment(sketch, "E327", {"start": v(-144.03, -24.4) * mm, "end": v(-146.86, -29.23) * mm});
            skLineSegment(sketch, "E328", {"start": v(-146.86, -29.23) * mm, "end": v(-148.27, -28.22) * mm});
            skLineSegment(sketch, "E329", {"start": v(-148.27, -28.22) * mm, "end": v(-148.27, -25) * mm});
            skLineSegment(sketch, "E330", {"start": v(-148.27, -25) * mm, "end": v(-149.68, -26.2) * mm});
            skLineSegment(sketch, "E331", {"start": v(-149.68, -26.2) * mm, "end": v(-151.9, -26.6) * mm});
            skLineSegment(sketch, "E332", {"start": v(-151.9, -26.6) * mm, "end": v(-152.3, -31.25) * mm});
            skLineSegment(sketch, "E333", {"start": v(-152.3, -31.25) * mm, "end": v(-154.72, -29.43) * mm});
            skLineSegment(sketch, "E334", {"start": v(-154.72, -29.43) * mm, "end": v(-159.96, -32.86) * mm});
            skLineSegment(sketch, "E335", {"start": v(-159.96, -32.86) * mm, "end": v(-161.98, -31.04) * mm});
            skLineSegment(sketch, "E336", {"start": v(-161.98, -31.04) * mm, "end": v(-165, -33.06) * mm});
            skLineSegment(sketch, "E337", {"start": v(-165, -33.06) * mm, "end": v(-166.41, -30.04) * mm});
            skLineSegment(sketch, "E338", {"start": v(-166.41, -30.04) * mm, "end": v(-171.25, -34.07) * mm});
            skLineSegment(sketch, "E339", {"start": v(-171.25, -34.07) * mm, "end": v(-173.06, -39.51) * mm});
            skLineSegment(sketch, "E340", {"start": v(-173.06, -39.51) * mm, "end": v(-177.1, -39.71) * mm});
            skLineSegment(sketch, "E341", {"start": v(-177.1, -39.71) * mm, "end": v(-176.29, -37.3) * mm});
            skLineSegment(sketch, "E342", {"start": v(-176.29, -37.3) * mm, "end": v(-176.49, -32.05) * mm});
            skLineSegment(sketch, "E343", {"start": v(-176.49, -32.05) * mm, "end": v(-173.67, -32.66) * mm});
            skLineSegment(sketch, "E344", {"start": v(-173.67, -32.66) * mm, "end": v(-171.25, -28.22) * mm});
            skLineSegment(sketch, "E345", {"start": v(-171.25, -28.22) * mm, "end": v(-166, -23.38) * mm});
            skLineSegment(sketch, "E346", {"start": v(-166, -23.38) * mm, "end": v(-164, -21.97) * mm});
            skLineSegment(sketch, "E347", {"start": v(-164, -21.97) * mm, "end": v(-164.2, -20.56) * mm});
            skLineSegment(sketch, "E348", {"start": v(-164.2, -20.56) * mm, "end": v(-168.43, -20.36) * mm});
            skLineSegment(sketch, "E349", {"start": v(-168.43, -20.36) * mm, "end": v(-170.44, -18.34) * mm});
            skLineSegment(sketch, "E350", {"start": v(-170.44, -18.34) * mm, "end": v(-168.43, -15.93) * mm});
            skLineSegment(sketch, "E351", {"start": v(-168.43, -15.93) * mm, "end": v(-165.8, -17.74) * mm});
            skLineSegment(sketch, "E352", {"start": v(-165.8, -17.74) * mm, "end": v(-154.52, -25.8) * mm});
            skLineSegment(sketch, "E353", {"start": v(-154.52, -25.8) * mm, "end": v(-152.1, -21.37) * mm});
            skLineSegment(sketch, "E354", {"start": v(-152.1, -21.37) * mm, "end": v(-151.7, -19.76) * mm});
            skLineSegment(sketch, "E355", {"start": v(-151.7, -19.76) * mm, "end": v(-149.68, -19.15) * mm});
            skLineSegment(sketch, "E356", {"start": v(-149.68, -19.15) * mm, "end": v(-157.14, -13.1) * mm});
            skLineSegment(sketch, "E357", {"start": v(-157.14, -13.1) * mm, "end": v(-165.2, -9.47) * mm});
            skLineSegment(sketch, "E358", {"start": v(-165.2, -9.47) * mm, "end": v(-173.06, -3.23) * mm});
            skLineSegment(sketch, "E359", {"start": v(-173.06, -3.23) * mm, "end": v(-176.49, 6.05) * mm});
            skLineSegment(sketch, "E360", {"start": v(-176.49, 6.05) * mm, "end": v(-176.9, 7.86) * mm});
            skLineSegment(sketch, "E361", {"start": v(-176.9, 7.86) * mm, "end": v(-177.3, 9.68) * mm});
            skLineSegment(sketch, "E362", {"start": v(-177.3, 9.68) * mm, "end": v(-173.87, 11.7) * mm});
            skLineSegment(sketch, "E363", {"start": v(-173.87, 11.7) * mm, "end": v(-173.47, 16.13) * mm});
            skLineSegment(sketch, "E364", {"start": v(-173.47, 16.13) * mm, "end": v(-174.68, 19.15) * mm});
            skLineSegment(sketch, "E365", {"start": v(-174.68, 19.15) * mm, "end": v(-179.51, 19.15) * mm});
            skLineSegment(sketch, "E366", {"start": v(-179.51, 19.15) * mm, "end": v(-182.13, 15.52) * mm});
            skLineSegment(sketch, "E367", {"start": v(-182.13, 15.52) * mm, "end": v(-184.15, 11.09) * mm});
            skLineSegment(sketch, "E368", {"start": v(-184.15, 11.09) * mm, "end": v(-185.96, 8.47) * mm});
            skLineSegment(sketch, "E369", {"start": v(-185.96, 8.47) * mm, "end": v(-187.17, 8.06) * mm});
            skLineSegment(sketch, "E370", {"start": v(-187.17, 8.06) * mm, "end": v(-190.4, 15.93) * mm});
            skLineSegment(sketch, "E371", {"start": v(-190.4, 15.93) * mm, "end": v(-191.2, 11.9) * mm});
            skLineSegment(sketch, "E372", {"start": v(-191.2, 11.9) * mm, "end": v(-194.43, 18.14) * mm});
            skLineSegment(sketch, "E373", {"start": v(-194.43, 18.14) * mm, "end": v(-194.43, 15.93) * mm});
            skLineSegment(sketch, "E374", {"start": v(-194.43, 15.93) * mm, "end": v(-190.2, 8.06) * mm});
            skLineSegment(sketch, "E375", {"start": v(-190.2, 8.06) * mm, "end": v(-190.6, 3.83) * mm});
            skLineSegment(sketch, "E376", {"start": v(-190.6, 3.83) * mm, "end": v(-192.01, 3.63) * mm});
            skLineSegment(sketch, "E377", {"start": v(-192.01, 3.63) * mm, "end": v(-192.62, -4.03) * mm});
            skLineSegment(sketch, "E378", {"start": v(-192.62, -4.03) * mm, "end": v(-188.99, -5.85) * mm});
            skLineSegment(sketch, "E379", {"start": v(-188.99, -5.85) * mm, "end": v(-191.6, -17.74) * mm});
            skLineSegment(sketch, "E380", {"start": v(-191.6, -17.74) * mm, "end": v(-210.56, -28.63) * mm});
            skLineSegment(sketch, "E381", {"start": v(-210.56, -28.63) * mm, "end": v(-192.42, -20.56) * mm});
            skLineSegment(sketch, "E382", {"start": v(-192.42, -20.56) * mm, "end": v(-195.44, -33.26) * mm});
            skLineSegment(sketch, "E383", {"start": v(-195.44, -33.26) * mm, "end": v(-199.87, -39.51) * mm});
            skLineSegment(sketch, "E384", {"start": v(-199.87, -39.51) * mm, "end": v(-205.32, -40.12) * mm});
            skLineSegment(sketch, "E385", {"start": v(-205.32, -40.12) * mm, "end": v(-207.94, -42.13) * mm});
            skLineSegment(sketch, "E386", {"start": v(-207.94, -42.13) * mm, "end": v(-211.36, -42.13) * mm});
            skLineSegment(sketch, "E387", {"start": v(-211.36, -42.13) * mm, "end": v(-215, -45.96) * mm});
            skLineSegment(sketch, "E388", {"start": v(-215, -45.96) * mm, "end": v(-218.02, -42.94) * mm});
            skLineSegment(sketch, "E389", {"start": v(-218.02, -42.94) * mm, "end": v(-218.02, -45.76) * mm});
            skLineSegment(sketch, "E390", {"start": v(-218.02, -45.76) * mm, "end": v(-222.65, -44.55) * mm});
            skLineSegment(sketch, "E391", {"start": v(-222.65, -44.55) * mm, "end": v(-220.44, -49.39) * mm});
            skLineSegment(sketch, "E392", {"start": v(-220.44, -49.39) * mm, "end": v(-72.27, -43.34) * mm});
            skLineSegment(sketch, "E393", {"start": v(-72.27, -43.34) * mm, "end": v(80.33, -42.74) * mm});
            skLineSegment(sketch, "E394", {"start": v(80.33, -42.74) * mm, "end": v(167.62, -43.74) * mm});
            skSolve(sketch);
        }
        {
            var Q0;
            Q0=makeQuery(id+"F0.imprint","IMPRINT",FACE,{"disambiguationData":[TD([[makeQuery(id+"F0.imprint","IMPRINT",EDGE,{"derivedFrom":sQuery(id+"F0.wireOp",EDGE,"E0")}),1.0]])]});
            extrude(context, id + "F1", {"entities" : qUnion([Q0]), "depth" : 5.83 * mm});
        }
    });
